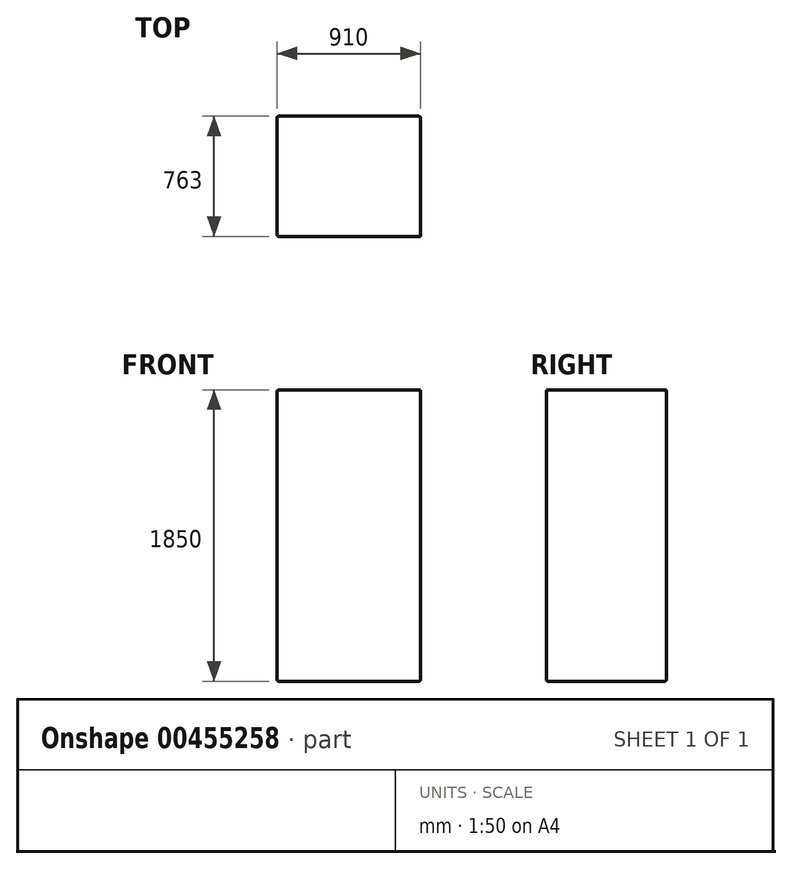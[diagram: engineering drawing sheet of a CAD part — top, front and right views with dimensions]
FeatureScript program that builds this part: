
annotation { "Feature Type Name" : "Feature", "Feature Type Description" : "" }
export const myFeature = defineFeature(function(context is Context, id is Id, definition is map)
    precondition{}
    {
        {
            var Q0;
            Q0=qCreatedBy(makeId("Top.planeOp"),FACE);
            var sketch = newSketch(context, id + "F0", { "sketchPlane" : qUnion([Q0])});
            skLineSegment(sketch, "E0.bottom", {"start": v(-495.64, 454.77) * mm, "end": v(414.36, 454.77) * mm});
            skLineSegment(sketch, "E0.top", {"start": v(-495.64, -308.23) * mm, "end": v(414.36, -308.23) * mm});
            skLineSegment(sketch, "E0.left", {"start": v(-495.64, 454.77) * mm, "end": v(-495.64, -308.23) * mm});
            skLineSegment(sketch, "E0.right", {"start": v(414.36, 454.77) * mm, "end": v(414.36, -308.23) * mm});
            skSolve(sketch);
        }
        {
            var Q0;
            Q0=makeQuery(id+"F0.imprint","IMPRINT",FACE,{"disambiguationData":[TD([[makeQuery(id+"F0.imprint","IMPRINT",EDGE,{"derivedFrom":sQuery(id+"F0.wireOp",EDGE,"E0.bottom")}),-1.0]])]});
            extrude(context, id + "F1", {"entities" : qUnion([Q0]), "depth" : 1850 * mm, "offsetDistance" : 25 * mm});
        }
        {
            var Q0;
            Q0=makeQuery(id+"F1.opExtrude","SWEPT_FACE",FACE,{"disambiguationData":[OSD([sQuery(id+"F0.wireOp",EDGE,"E0.bottom")])]});
            var Q1;
            Q1=makeQuery(id+"F1.opExtrude","SWEPT_FACE",FACE,{"disambiguationData":[OSD([sQuery(id+"F0.wireOp",EDGE,"E0.left")])]});
            var Q2;
            Q2=makeQuery(id+"F1.opExtrude","CAP_FACE",FACE,{"disambiguationData":[OSD([sQuery(id+"F0.wireOp",EDGE,"E0.bottom"),sQuery(id+"F0.wireOp",EDGE,"E0.top"),sQuery(id+"F0.wireOp",EDGE,"E0.left"),sQuery(id+"F0.wireOp",EDGE,"E0.right")])],"isStart":true});
            fillet(context, id + "F2", {"entities" : qUnion([Q0, Q1, Q2]), "radius" : 10 * mm, "tangentPropagation" : true, "allowEdgeOverflow" : false});
        }
    });
